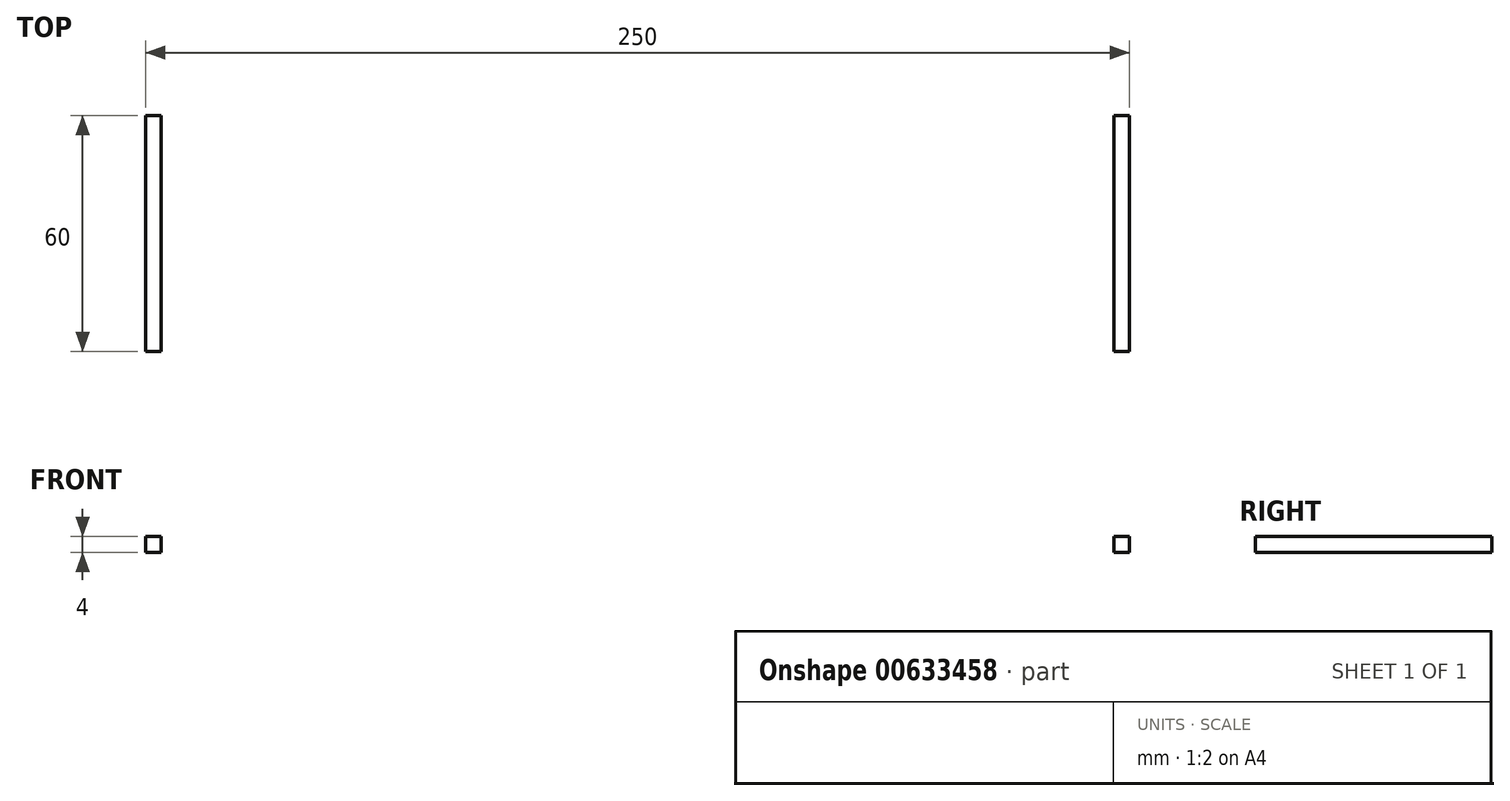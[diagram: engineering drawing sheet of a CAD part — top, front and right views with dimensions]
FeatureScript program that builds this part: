
annotation { "Feature Type Name" : "Feature", "Feature Type Description" : "" }
export const myFeature = defineFeature(function(context is Context, id is Id, definition is map)
    precondition{}
    {
        {
            var Q0;
            Q0=qCreatedBy(makeId("Top.planeOp"),FACE);
            var sketch = newSketch(context, id + "F0", { "sketchPlane" : qUnion([Q0])});
            skLineSegment(sketch, "E0.bottom", {"start": v(0, 0) * mm, "end": v(-250, 0) * mm});
            skLineSegment(sketch, "E0.top", {"start": v(0, 300) * mm, "end": v(-250, 300) * mm});
            skLineSegment(sketch, "E0.left", {"start": v(0, 0) * mm, "end": v(0, 300) * mm});
            skLineSegment(sketch, "E0.right", {"start": v(-250, 0) * mm, "end": v(-250, 300) * mm});
            skLineSegment(sketch, "E1.bottom", {"start": v(-250, 300) * mm, "end": v(-246, 300) * mm});
            skLineSegment(sketch, "E1.top", {"start": v(-250, 240) * mm, "end": v(-246, 240) * mm});
            skLineSegment(sketch, "E1.left", {"start": v(-250, 300) * mm, "end": v(-250, 240) * mm});
            skLineSegment(sketch, "E1.right", {"start": v(-246, 300) * mm, "end": v(-246, 240) * mm});
            skLineSegment(sketch, "E2.bottom", {"start": v(-250, 0) * mm, "end": v(-246, 0) * mm});
            skLineSegment(sketch, "E2.top", {"start": v(-250, 60) * mm, "end": v(-246, 60) * mm});
            skLineSegment(sketch, "E2.left", {"start": v(-250, 0) * mm, "end": v(-250, 60) * mm});
            skLineSegment(sketch, "E2.right", {"start": v(-246, 0) * mm, "end": v(-246, 60) * mm});
            skLineSegment(sketch, "E3.bottom", {"start": v(-250, 180) * mm, "end": v(-246, 180) * mm});
            skLineSegment(sketch, "E3.top", {"start": v(-250, 120) * mm, "end": v(-246, 120) * mm});
            skLineSegment(sketch, "E3.left", {"start": v(-250, 180) * mm, "end": v(-250, 120) * mm});
            skLineSegment(sketch, "E3.right", {"start": v(-246, 180) * mm, "end": v(-246, 120) * mm});
            skLineSegment(sketch, "E4.bottom", {"start": v(0, 300) * mm, "end": v(-4, 300) * mm});
            skLineSegment(sketch, "E4.top", {"start": v(0, 240) * mm, "end": v(-4, 240) * mm});
            skLineSegment(sketch, "E4.left", {"start": v(0, 300) * mm, "end": v(0, 240) * mm});
            skLineSegment(sketch, "E4.right", {"start": v(-4, 300) * mm, "end": v(-4, 240) * mm});
            skLineSegment(sketch, "E5.bottom", {"start": v(0, 180) * mm, "end": v(-4, 180) * mm});
            skLineSegment(sketch, "E5.top", {"start": v(0, 120) * mm, "end": v(-4, 120) * mm});
            skLineSegment(sketch, "E5.left", {"start": v(0, 180) * mm, "end": v(0, 120) * mm});
            skLineSegment(sketch, "E5.right", {"start": v(-4, 180) * mm, "end": v(-4, 120) * mm});
            skLineSegment(sketch, "E6.bottom", {"start": v(0, 0) * mm, "end": v(-4, 0) * mm});
            skLineSegment(sketch, "E6.top", {"start": v(0, 60) * mm, "end": v(-4, 60) * mm});
            skLineSegment(sketch, "E6.left", {"start": v(0, 0) * mm, "end": v(0, 60) * mm});
            skLineSegment(sketch, "E6.right", {"start": v(-4, 0) * mm, "end": v(-4, 60) * mm});
            skLineSegment(sketch, "E7.bottom", {"start": v(-246, 300) * mm, "end": v(-196, 300) * mm});
            skLineSegment(sketch, "E7.top", {"start": v(-246, 296) * mm, "end": v(-196, 296) * mm});
            skLineSegment(sketch, "E7.left", {"start": v(-246, 300) * mm, "end": v(-246, 296) * mm});
            skLineSegment(sketch, "E7.right", {"start": v(-196, 300) * mm, "end": v(-196, 296) * mm});
            skLineSegment(sketch, "E8.bottom", {"start": v(-146, 300) * mm, "end": v(-104, 300) * mm});
            skLineSegment(sketch, "E8.top", {"start": v(-146, 296) * mm, "end": v(-104, 296) * mm});
            skLineSegment(sketch, "E8.left", {"start": v(-146, 300) * mm, "end": v(-146, 296) * mm});
            skLineSegment(sketch, "E8.right", {"start": v(-104, 300) * mm, "end": v(-104, 296) * mm});
            skLineSegment(sketch, "E9.bottom", {"start": v(-4, 300) * mm, "end": v(-54, 300) * mm});
            skLineSegment(sketch, "E9.top", {"start": v(-4, 296) * mm, "end": v(-54, 296) * mm});
            skLineSegment(sketch, "E9.left", {"start": v(-4, 300) * mm, "end": v(-4, 296) * mm});
            skLineSegment(sketch, "E9.right", {"start": v(-54, 300) * mm, "end": v(-54, 296) * mm});
            skSolve(sketch);
        }
        {
            var Q0;
            Q0=makeQuery(id+"F0.imprint","IMPRINT",FACE,{"disambiguationData":[TD([[makeQuery(id+"F0.imprint","IMPRINT",EDGE,{"derivedFrom":sQuery(id+"F0.wireOp",EDGE,"E0.bottom")}),-1.0]])]});
            extrude(context, id + "F1", {"entities" : qUnion([Q0]), "depth" : 4 * mm, "offsetDistance" : 25 * mm});
        }
    });
